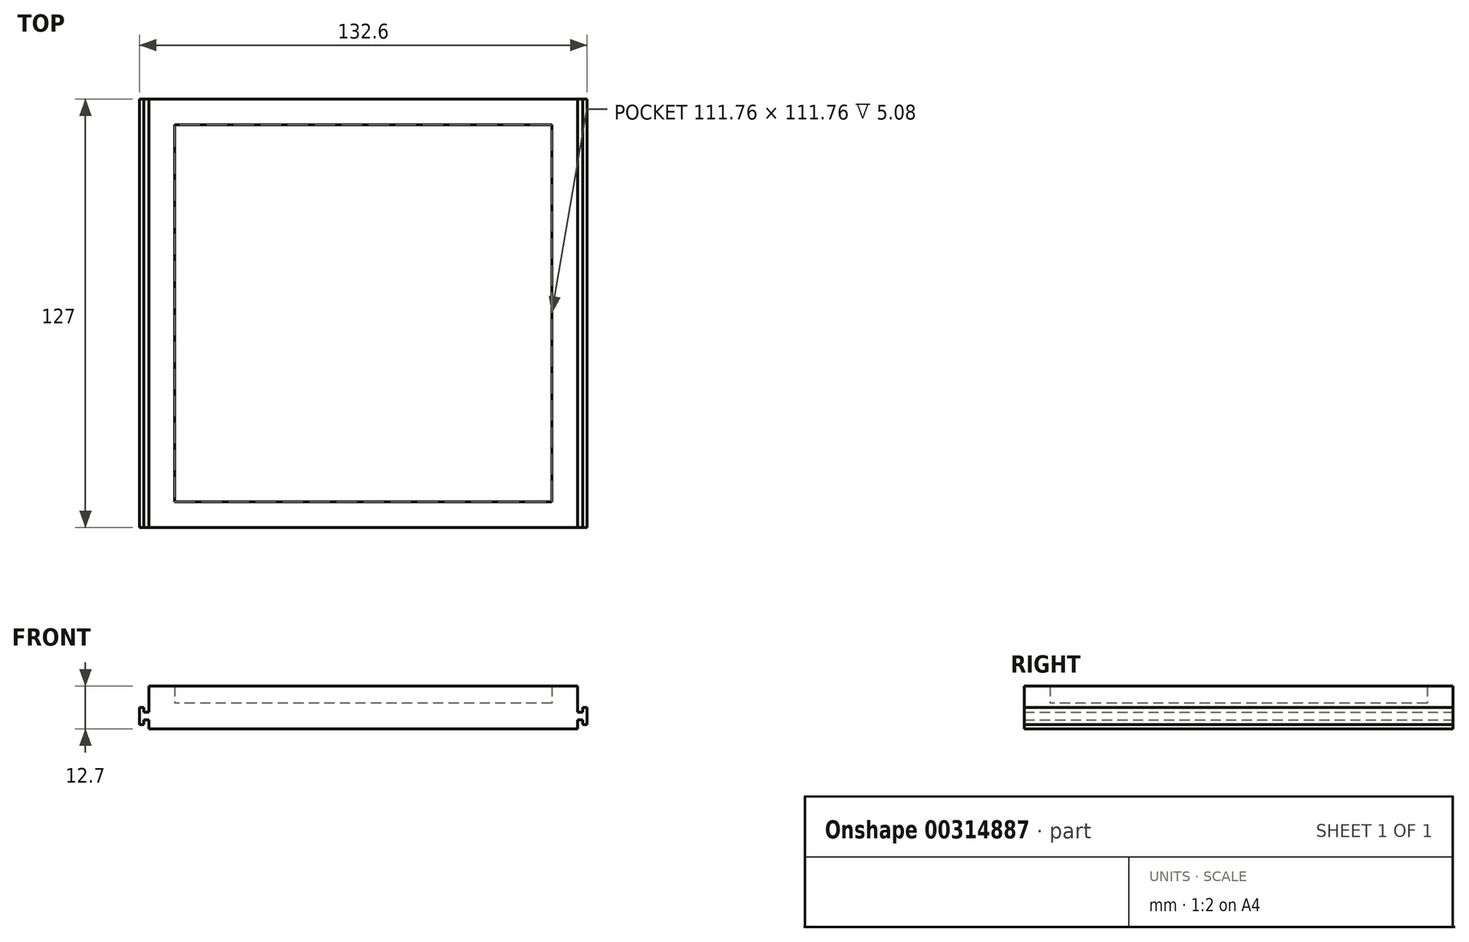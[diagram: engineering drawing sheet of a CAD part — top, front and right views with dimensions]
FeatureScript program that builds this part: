
annotation { "Feature Type Name" : "Feature", "Feature Type Description" : "" }
export const myFeature = defineFeature(function(context is Context, id is Id, definition is map)
    precondition{}
    {
        {
            var Q0;
            Q0=qCreatedBy(makeId("Top.planeOp"),FACE);
            var sketch = newSketch(context, id + "F0", { "sketchPlane" : qUnion([Q0])});
            skLineSegment(sketch, "E0.bottom", {"start": v(63.5, 63.5) * mm, "end": v(-63.5, 63.5) * mm});
            skLineSegment(sketch, "E0.top", {"start": v(63.5, -63.5) * mm, "end": v(-63.5, -63.5) * mm});
            skLineSegment(sketch, "E0.left", {"start": v(63.5, 63.5) * mm, "end": v(63.5, -63.5) * mm});
            skLineSegment(sketch, "E0.right", {"start": v(-63.5, 63.5) * mm, "end": v(-63.5, -63.5) * mm});
            skPoint(sketch, "E0.middle", {"position": v(0, 0) * mm});
            skSolve(sketch);
        }
        {
            var Q0;
            Q0 = qSketchRegion(id + "F0", true);
            extrude(context, id + "F1", {"entities" : qUnion([Q0]), "depth" : 12.7 * mm});
        }
        {
            var Q0;
            Q0=makeQuery(id+"F1.opExtrude","CAP_FACE",FACE,{"disambiguationData":[OSD([sQuery(id+"F0.wireOp",EDGE,"E0.bottom"),sQuery(id+"F0.wireOp",EDGE,"E0.top"),sQuery(id+"F0.wireOp",EDGE,"E0.left"),sQuery(id+"F0.wireOp",EDGE,"E0.right")])],"isStart":false});
            shell(context, id + "F2", {"entities" : qUnion([Q0]), "thickness" : 7.62 * mm});
        }
        {
            var Q0;
            Q0=qCreatedBy(makeId("Front.planeOp"),FACE);
            var sketch = newSketch(context, id + "F3", { "sketchPlane" : qUnion([Q0])});
            skLineSegment(sketch, "E1.MirrorCS", {"start": v(-65.03, 4.95) * mm, "end": v(-65.03, 2.67) * mm});
            skPoint(sketch, "E2.MirrorP", {"position": v(-65.03, 3.81) * mm});
            skLineSegment(sketch, "E3.MirrorCS", {"start": v(-65.03, 6.35) * mm, "end": v(-65.03, 1.27) * mm});
            skLineSegment(sketch, "E4.MirrorCS", {"start": v(-66.3, 6.35) * mm, "end": v(-66.3, 1.27) * mm});
            skLineSegment(sketch, "E5.MirrorCS", {"start": v(-63.5, 4.95) * mm, "end": v(-65.03, 4.95) * mm});
            skLineSegment(sketch, "E6.MirrorCS", {"start": v(-65.03, 1.27) * mm, "end": v(-66.3, 1.27) * mm});
            skLineSegment(sketch, "E7.MirrorCS", {"start": v(-63.5, 2.67) * mm, "end": v(-65.03, 2.67) * mm});
            skLineSegment(sketch, "E8.MirrorCS", {"start": v(-63.5, 4.95) * mm, "end": v(-63.5, 2.67) * mm});
            skLineSegment(sketch, "E9.MirrorCS", {"start": v(-65.03, 6.35) * mm, "end": v(-66.3, 6.35) * mm});
            skLineSegment(sketch, "E10", {"start": v(-63.5, 0) * mm, "end": v(-63.5, 3.81) * mm});
            skPoint(sketch, "E11", {"position": v(-63.5, 3.81) * mm});
            skLineSegment(sketch, "E12.MirrorCS", {"start": v(65.03, 4.95) * mm, "end": v(65.03, 2.67) * mm});
            skLineSegment(sketch, "E13.MirrorCS", {"start": v(63.5, 2.67) * mm, "end": v(65.03, 2.67) * mm});
            skLineSegment(sketch, "E14.MirrorCS", {"start": v(65.03, 1.27) * mm, "end": v(66.3, 1.27) * mm});
            skLineSegment(sketch, "E15.MirrorCS", {"start": v(63.5, 4.95) * mm, "end": v(65.03, 4.95) * mm});
            skLineSegment(sketch, "E16.MirrorCS", {"start": v(66.3, 6.35) * mm, "end": v(66.3, 1.27) * mm});
            skLineSegment(sketch, "E17.MirrorCS", {"start": v(65.03, 6.35) * mm, "end": v(65.03, 1.27) * mm});
            skLineSegment(sketch, "E18.MirrorCS", {"start": v(63.5, 0) * mm, "end": v(63.5, 3.81) * mm});
            skLineSegment(sketch, "E19.MirrorCS", {"start": v(63.5, 4.95) * mm, "end": v(63.5, 2.67) * mm});
            skLineSegment(sketch, "E20.MirrorCS", {"start": v(65.03, 6.35) * mm, "end": v(66.3, 6.35) * mm});
            skPoint(sketch, "E21.MirrorP", {"position": v(65.03, 3.81) * mm});
            skPoint(sketch, "E22.MirrorP", {"position": v(63.5, 3.81) * mm});
            skSolve(sketch);
        }
        {
            var Q0;
            Q0 = qSketchRegion(id + "F3", true);
            extrude(context, id + "F4", {"entities" : qUnion([Q0]), "operationType" : NewBodyOperationType.ADD, "endBound" : BoundingType.SYMMETRIC, "depth" : 127 * mm});
        }
    });
